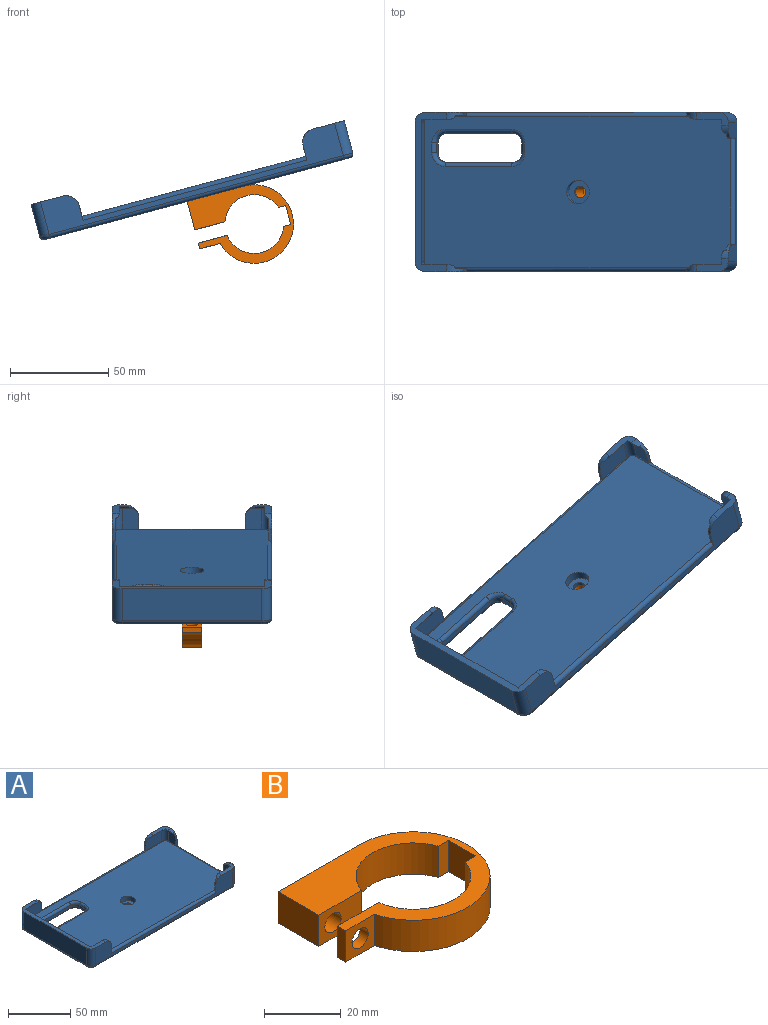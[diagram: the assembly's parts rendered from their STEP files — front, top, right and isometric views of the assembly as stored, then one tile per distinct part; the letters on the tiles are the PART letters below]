
ASSEMBLY  parts=2 mates=1
PART A: 88 faces, bbox 165.8x81.8x19 mm
  f0: plane 161.5x77mm, normal (0,0,1), area 11429.3mm2, adj f26,f28,f30,f32,f33,f51,f69,f70
  f1: plane 161x77mm, normal (0,0,-1), area 11472.1mm2, adj f52,f61,f62,f63,f64,f65,f66,f67
  f2: plane 16.5x6.5mm, normal (0,0,1), area 62.9mm2, adj f8,f9,f15,f16,f23,f45,f49
  f3: plane 16.5x6.5mm, normal (0,0,1), area 62.9mm2, adj f7,f8,f14,f22,f35,f44,f47
  f4: plane 81x16.5mm, normal (0,0,1), area 363.8mm2, adj f7,f9,f20,f21,f24,f34,f36,f37
  f5: plane 16.49x0.06mm, normal (0,0,-1), area 1mm2, adj f11,f16,f28,f49
  f6: plane 16.49x0.06mm, normal (0,0,-1), area 1mm2, adj f13,f14,f30,f47
  f7: plane 155x17mm, normal (0,-1,0), area 903mm2, adj f3,f4,f21,f22,f42,f43,f46,f47
  f8: plane 71x17mm, normal (1,0,0), area 403mm2, adj f2,f3,f22,f23,f40,f41,f44,f45
  f9: plane 155x17mm, normal (0,1,0), area 903mm2, adj f2,f4,f23,f24,f38,f39,f48,f49
  f10: plane 6.49x0.06mm, normal (0,0,-1), area 0.4mm2, adj f12,f15,f28,f45
  f11: plane 18.5x11.06mm, normal (0,-1,0), area 200.2mm2, adj f5,f28,f39,f49,f87
  f12: plane 11.06x8.5mm, normal (-1,0,0), area 89.6mm2, adj f10,f28,f40,f45,f85
  f13: plane 18.5x11.06mm, normal (0,1,0), area 200.2mm2, adj f6,f30,f43,f47,f86
  f14: cylinder r=2mm len=18.31mm, axis (1,0,0), area 44.2mm2, adj f3,f6,f30,f35,f47
  f15: cylinder r=2mm len=8.31mm, axis (0,-1,0), area 17.8mm2, adj f2,f10,f16,f28,f45
  f16: cylinder r=2mm len=18.31mm, axis (1,0,0), area 44.2mm2, adj f2,f5,f15,f28,f49
  f17: plane 16.49x0.06mm, normal (0,0,-1), area 1mm2, adj f26,f27,f37,f48
  f18: plane 72.33x0.06mm, normal (0,0,-1), area 4.6mm2, adj f26,f32,f33,f36
  f19: plane 16.49x0.06mm, normal (0,0,-1), area 1mm2, adj f31,f32,f34,f46
  f20: plane 71x17mm, normal (-1,0,0), area 1207mm2, adj f4,f21,f24,f81
  f21: cylinder r=5mm len=17mm, axis (0,0,-1), area 133.5mm2, adj f4,f7,f20,f79
  f22: cylinder r=5mm len=17mm, axis (0,0,-1), area 133.5mm2, adj f3,f7,f8,f78
  f23: cylinder r=5mm len=17mm, axis (0,0,-1), area 133.5mm2, adj f2,f8,f9,f82
  f24: cylinder r=5mm len=17mm, axis (0,0,-1), area 133.5mm2, adj f4,f9,f20,f83
  f25: plane 6.49x0.06mm, normal (0,0,-1), area 0.4mm2, adj f29,f30,f35,f44
  f26: cylinder r=3.5mm len=11.31mm, axis (0,0,-1), area 60.8mm2, adj f0,f17,f18,f27,f33,f36,f37,f87
  f27: plane 18.5x11.06mm, normal (0,-1,0), area 200.2mm2, adj f17,f26,f38,f48,f87
  f28: cylinder r=3.5mm len=11.31mm, axis (0,0,-1), area 60.8mm2, adj f0,f5,f10,f11,f12,f15,f16,f85
  f29: plane 11.06x8.5mm, normal (-1,0,0), area 89.6mm2, adj f25,f30,f41,f44,f85
  f30: cylinder r=3.5mm len=11.31mm, axis (0,0,-1), area 60.8mm2, adj f0,f6,f13,f14,f25,f29,f35,f85
  f31: plane 18.5x11.06mm, normal (0,1,0), area 200.2mm2, adj f19,f32,f42,f46,f86
  f32: cylinder r=3.5mm len=11.31mm, axis (0,0,-1), area 60.8mm2, adj f0,f18,f19,f31,f33,f34,f36,f86
  f33: plane 71x11mm, normal (1,0,0), area 781mm2, adj f0,f18,f26,f32
  f34: cylinder r=2mm len=18.31mm, axis (1,0,0), area 44.2mm2, adj f4,f19,f32,f36,f46
  f35: cylinder r=2mm len=8.31mm, axis (0,-1,0), area 17.8mm2, adj f3,f14,f25,f30,f44
  f36: cylinder r=2mm len=75.95mm, axis (0,-1,0), area 197mm2, adj f4,f18,f26,f32,f34,f37
  f37: cylinder r=2mm len=18.31mm, axis (1,0,0), area 44.2mm2, adj f4,f17,f26,f36,f48
  f38: plane 7.5x1.5mm, normal (1,0,0), area 9.1mm2, adj f9,f27,f48,f87
  f39: plane 7.5x1.5mm, normal (-1,0,0), area 9.1mm2, adj f9,f11,f49,f87
  f40: plane 7.5x1.5mm, normal (0,-1,0), area 9.1mm2, adj f8,f12,f45,f85
  f41: plane 7.5x1.5mm, normal (0,1,0), area 9.1mm2, adj f8,f29,f44,f85
  f42: plane 7.5x1.5mm, normal (1,0,0), area 9.1mm2, adj f7,f31,f46,f86
  f43: plane 7.5x1.5mm, normal (-1,0,0), area 9.1mm2, adj f7,f13,f47,f86
  f44: cylinder r=7mm len=7mm, axis (-1,0,0), area 24.4mm2, adj f3,f8,f25,f29,f35,f41
  f45: cylinder r=7mm len=7mm, axis (1,0,0), area 24.4mm2, adj f2,f8,f10,f12,f15,f40
  f46: cylinder r=7mm len=7mm, axis (0,1,0), area 24.4mm2, adj f4,f7,f19,f31,f34,f42
  f47: cylinder r=7mm len=7mm, axis (0,-1,0), area 24.4mm2, adj f3,f6,f7,f13,f14,f43
  f48: cylinder r=7mm len=7mm, axis (0,1,0), area 24.4mm2, adj f4,f9,f17,f27,f37,f38
  f49: cylinder r=7mm len=7mm, axis (0,-1,0), area 24.4mm2, adj f2,f5,f9,f11,f16,f39
  f50: plane 12x12mm, normal (0,0,1), area 84.8mm2, adj f51,f52
  f51: cylinder r=6mm len=12mm, axis (0,0,1), area 169.6mm2, adj f0,f50
  f52: cylinder r=3mm len=6mm, axis (0,0,1), area 37.7mm2, adj f1,f50
  f53: plane 5x2.5mm, normal (1,0,0), area 12.5mm2, adj f54,f60,f64,f73
  f54: cylinder r=5mm len=5mm, axis (0,0,1), area 19.6mm2, adj f53,f55,f62,f75
  f55: plane 35x2.5mm, normal (0,1,0), area 87.5mm2, adj f54,f56,f61,f76
  f56: cylinder r=5mm len=5mm, axis (0,0,1), area 19.6mm2, adj f55,f57,f63,f74
  f57: plane 5x2.5mm, normal (-1,0,0), area 12.5mm2, adj f56,f58,f65,f72
  f58: cylinder r=5mm len=5mm, axis (0,0,1), area 19.6mm2, adj f57,f59,f67,f70
  f59: plane 35x2.5mm, normal (0,-1,0), area 87.5mm2, adj f58,f60,f68,f69
  f60: cylinder r=5mm len=5mm, axis (0,0,1), area 19.6mm2, adj f53,f59,f66,f71
  f61: cylinder r=2mm len=35mm, axis (-1,0,0), area 110mm2, adj f1,f55,f62,f63
  f62: torus R=7mm, axis (0,0,1), area 28.3mm2, adj f1,f54,f61,f64
  f63: torus R=7mm, axis (0,0,1), area 28.3mm2, adj f1,f56,f61,f65
  f64: cylinder r=2mm len=5mm, axis (0,1,0), area 15.7mm2, adj f1,f53,f62,f66
  f65: cylinder r=2mm len=5mm, axis (0,-1,0), area 15.7mm2, adj f1,f57,f63,f67
  f66: torus R=7mm, axis (0,0,1), area 28.3mm2, adj f1,f60,f64,f68
  f67: torus R=7mm, axis (0,0,1), area 28.3mm2, adj f1,f58,f65,f68
  f68: cylinder r=2mm len=35mm, axis (1,0,0), area 110mm2, adj f1,f59,f66,f67
  f69: cylinder r=2mm len=35mm, axis (1,0,0), area 110mm2, adj f0,f59,f70,f71
  f70: torus R=7mm, axis (0,0,1), area 28.3mm2, adj f0,f58,f69,f72
  f71: torus R=7mm, axis (0,0,1), area 28.3mm2, adj f0,f60,f69,f73
  f72: cylinder r=2mm len=5mm, axis (0,-1,0), area 15.7mm2, adj f0,f57,f70,f74
  f73: cylinder r=2mm len=5mm, axis (0,1,0), area 15.7mm2, adj f0,f53,f71,f75
  f74: torus R=7mm, axis (0,0,1), area 28.3mm2, adj f0,f56,f72,f76
  f75: torus R=7mm, axis (0,0,1), area 28.3mm2, adj f0,f54,f73,f76
  f76: cylinder r=2mm len=35mm, axis (-1,0,0), area 110mm2, adj f0,f55,f74,f75
  f77: cylinder r=2mm len=155mm, axis (1,0,0), area 486.9mm2, adj f1,f7,f78,f79
  f78: torus R=3mm, axis (0,0,1), area 21.1mm2, adj f1,f22,f77,f80
  f79: torus R=3mm, axis (0,0,1), area 21.1mm2, adj f1,f21,f77,f81
  f80: cylinder r=2mm len=71mm, axis (0,1,0), area 223.1mm2, adj f1,f8,f78,f82
  f81: cylinder r=2mm len=71mm, axis (0,-1,0), area 223.1mm2, adj f1,f20,f79,f83
  f82: torus R=3mm, axis (0,0,1), area 21.1mm2, adj f1,f23,f80,f84
  f83: torus R=3mm, axis (0,0,1), area 21.1mm2, adj f1,f24,f81,f84
  f84: cylinder r=2mm len=155mm, axis (-1,0,0), area 486.9mm2, adj f1,f9,f82,f83
  f85: cylinder r=2mm len=74.61mm, axis (0,1,0), area 179.5mm2, adj f0,f8,f12,f28,f29,f30,f40,f41
  f86: cylinder r=2mm len=158.61mm, axis (1,0,0), area 390.6mm2, adj f0,f7,f13,f30,f31,f32,f42,f43
  f87: cylinder r=2mm len=158.61mm, axis (-1,0,0), area 390.6mm2, adj f0,f9,f11,f26,f27,f28,f38,f39
PART B: 16 faces, bbox 50x40x10 mm
  f0: plane 15x10mm, normal (-1,0,0), area 150mm2, adj f1,f11,f12,f13
  f1: plane 15.86x10mm, normal (0,-1,0), area 130.3mm2, adj f0,f2,f12,f13,f14
  f2: cylinder r=15mm len=28.28mm, axis (0,0,-1), area 369.3mm2, adj f1,f3,f12,f13
  f3: plane 10x3.72mm, normal (0,-1,0), area 37.2mm2, adj f2,f4,f12,f13
  f4: plane 10x10mm, normal (-1,0,0), area 100mm2, adj f3,f5,f12,f13
  f5: plane 10x3.72mm, normal (0,1,0), area 37.2mm2, adj f4,f6,f12,f13
  f6: cylinder r=15mm len=29.01mm, axis (0,0,-1), area 400.2mm2, adj f5,f7,f12,f13
  f7: plane 15.13x10mm, normal (0,1,0), area 123.1mm2, adj f6,f8,f12,f13,f15
  f8: plane 10x3mm, normal (-1,0,0), area 30mm2, adj f7,f9,f12,f13
  f9: plane 10.64x10mm, normal (0,-1,0), area 78.1mm2, adj f8,f10,f12,f13,f15
  f10: cylinder r=20mm len=40mm, axis (0,0,-1), area 891.9mm2, adj f9,f11,f12,f13
  f11: plane 30x10mm, normal (0,1,0), area 271.7mm2, adj f0,f10,f12,f13,f14
  f12: plane 50x40mm, normal (0,0,1), area 748.7mm2, adj f0,f1,f2,f3,f4,f5,f6,f7
  f13: plane 50x40mm, normal (0,0,-1), area 748.7mm2, adj f0,f1,f2,f3,f4,f5,f6,f7
  f14: cylinder r=3mm len=15mm, axis (0,-1,0), area 282.7mm2, adj f1,f11
  f15: cylinder r=3mm len=6mm, axis (0,-1,0), area 56.5mm2, adj f7,f9
PLACE A rot(axis=(0,-1,0),15deg) t=(-3.61,0,-1.95)mm
PLACE B rot(axis=(0.98,-0.13,0.13),91deg) t=(26.71,5,-19.71)mm
MATE revolute B.f14 <-> A.f52  axis (-0.26,0,0.97) through (-2.31,0,-6.78)mm
